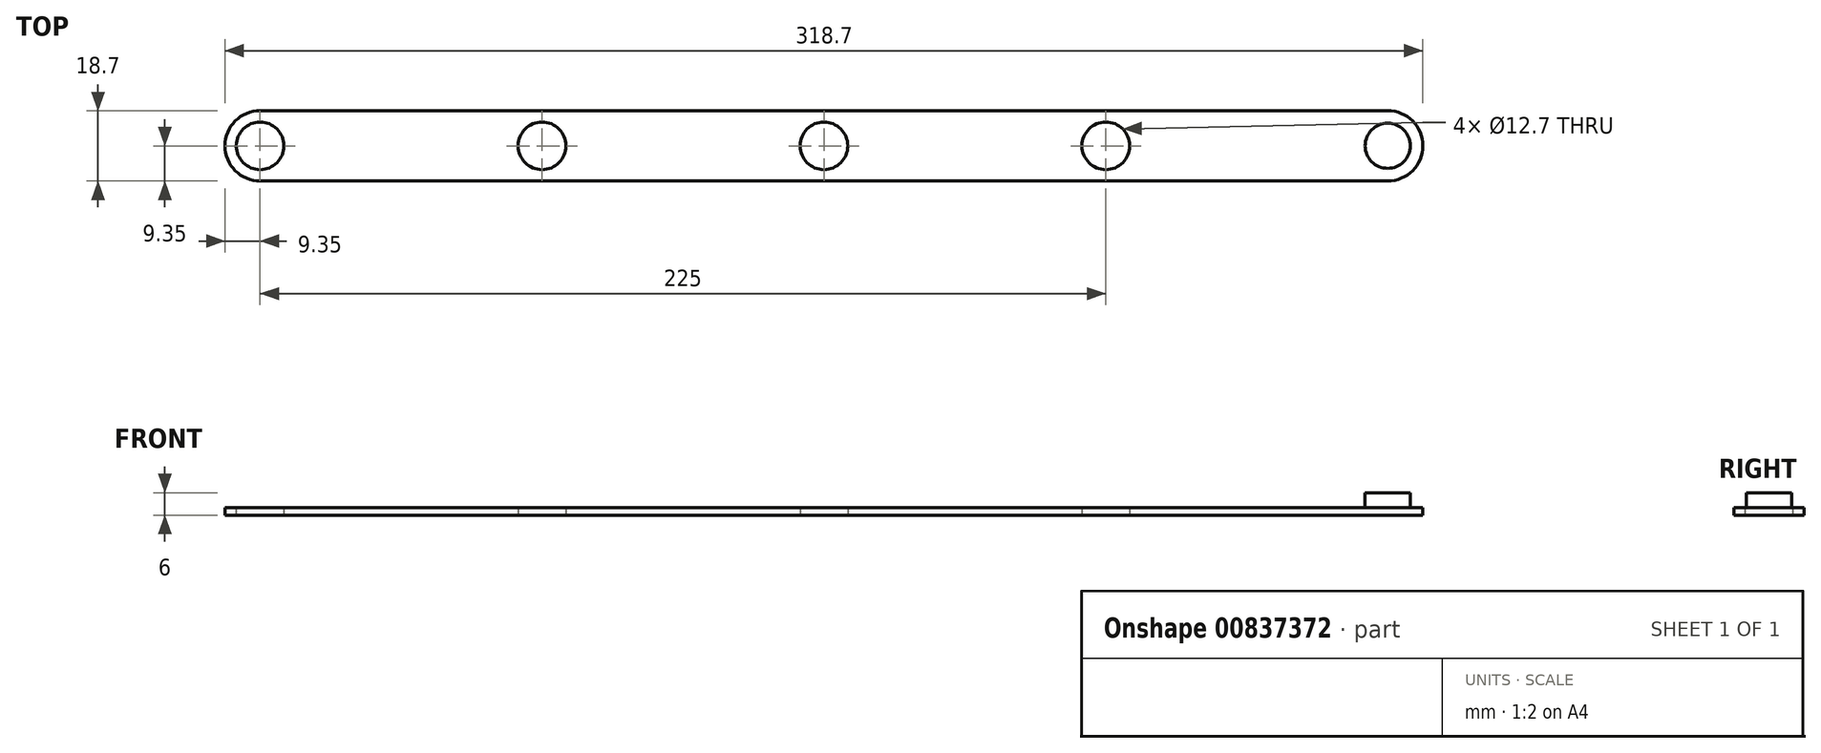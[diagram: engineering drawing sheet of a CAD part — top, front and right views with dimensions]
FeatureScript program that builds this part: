
annotation { "Feature Type Name" : "Feature", "Feature Type Description" : "" }
export const myFeature = defineFeature(function(context is Context, id is Id, definition is map)
    precondition{}
    {
        {
            var Q0;
            Q0=qCreatedBy(makeId("Top.planeOp"),FACE);
            var sketch = newSketch(context, id + "F0", { "sketchPlane" : qUnion([Q0])});
            skCircle(sketch, "E0", {"center": v(0, 0) * mm, "radius": 6 * mm});
            skLineSegment(sketch, "E1", {"start": v(0, 0) * mm, "end": v(-75, 0) * mm});
            skCircle(sketch, "E2", {"center": v(-75, 0) * mm, "radius": 6.35 * mm});
            skLineSegment(sketch, "E3", {"start": v(-75, 0) * mm, "end": v(-150, 0) * mm});
            skLineSegment(sketch, "E4", {"start": v(-150, 0) * mm, "end": v(-225, 0) * mm});
            skCircle(sketch, "E5", {"center": v(-150, 0) * mm, "radius": 6.35 * mm});
            skCircle(sketch, "E6", {"center": v(-225, 0) * mm, "radius": 6.35 * mm});
            skLineSegment(sketch, "E7", {"start": v(-225, 0) * mm, "end": v(-300, 0) * mm});
            skCircle(sketch, "E8", {"center": v(-300, 0) * mm, "radius": 6.35 * mm});
            skArc(sketch, "E9.0", {"start": v(-300, 9.35) * mm, "mid": v(-309.35, 0) * mm, "end": v(-300, -9.35) * mm});
            skPoint(sketch, "E10.orphan", {"position": v(-64.07, -9.35) * mm});
            skPoint(sketch, "E11.end.orphan", {"position": v(30, -9.35) * mm});
            skLineSegment(sketch, "E12", {"start": v(-300, 9.35) * mm, "end": v(0, 9.35) * mm});
            skLineSegment(sketch, "E13", {"start": v(-300, -9.35) * mm, "end": v(0, -9.35) * mm});
            skArc(sketch, "E14", {"start": v(0, -9.35) * mm, "mid": v(9.35, 0) * mm, "end": v(0, 9.35) * mm});
            skSolve(sketch);
        }
        {
            var Q0;
            Q0 = qSketchRegion(id + "F0", true);
            extrude(context, id + "F1", {"entities" : qUnion([Q0]), "depth" : 2 * mm, "offsetDistance" : 25 * mm});
        }
        {
            var Q0;
            Q0=makeQuery(id+"F0.imprint","IMPRINT",FACE,{"disambiguationData":[TD([[makeQuery(id+"F0.imprint","IMPRINT",EDGE,{"derivedFrom":sQuery(id+"F0.wireOp",EDGE,"E0")}),1.0]])]});
            extrude(context, id + "F2", {"entities" : qUnion([Q0]), "operationType" : NewBodyOperationType.ADD, "depth" : 6 * mm, "offsetDistance" : 25 * mm});
        }
    });
